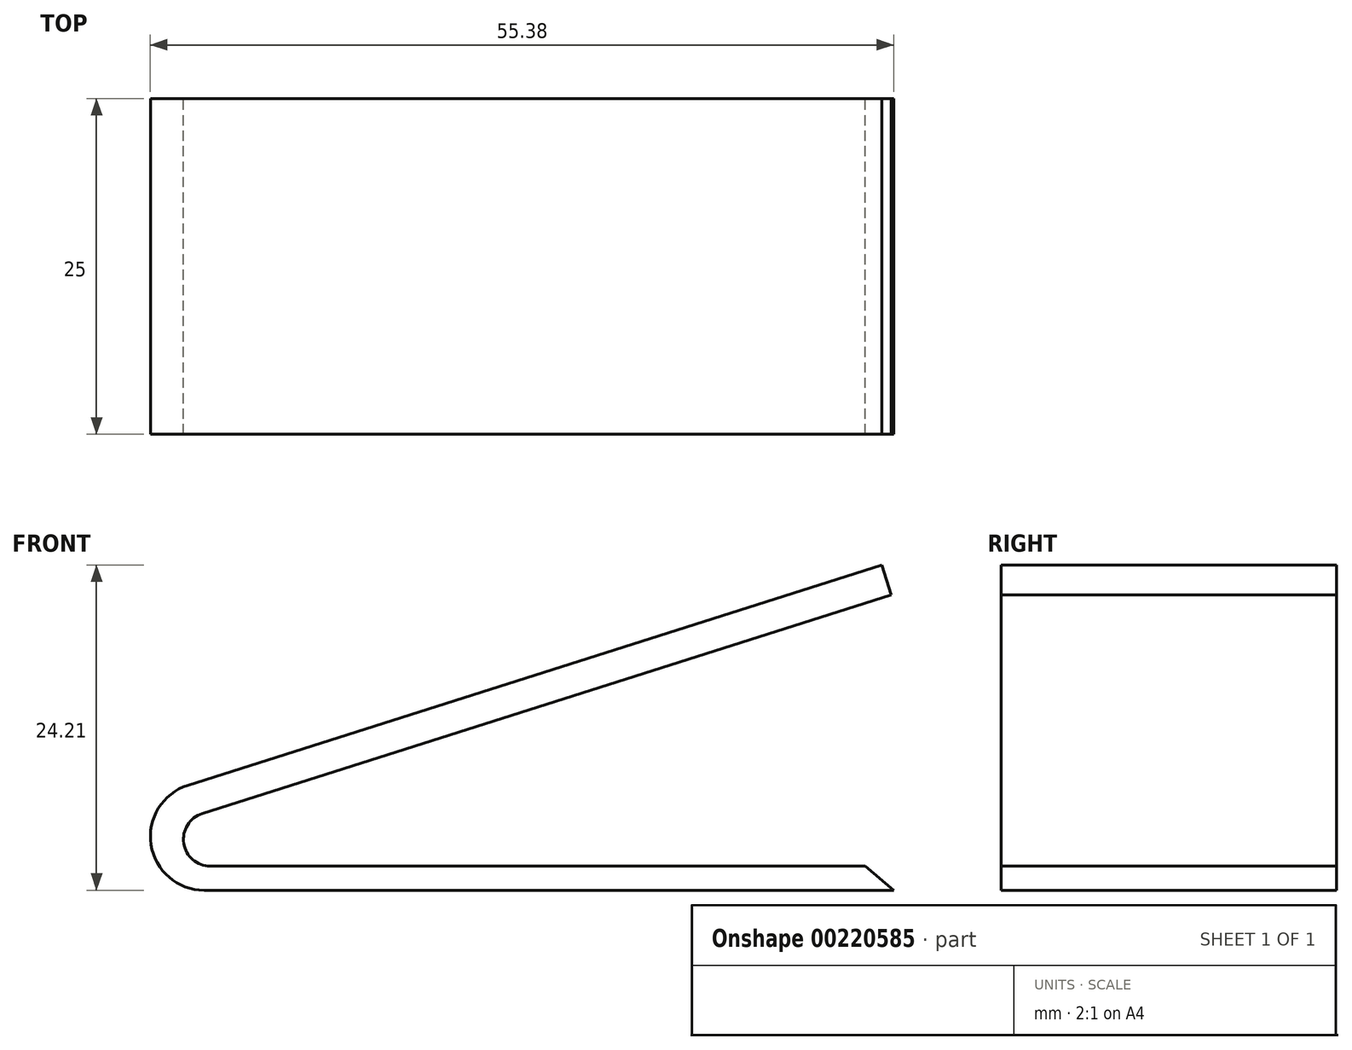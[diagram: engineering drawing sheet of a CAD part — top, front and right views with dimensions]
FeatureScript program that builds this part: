
annotation { "Feature Type Name" : "Feature", "Feature Type Description" : "" }
export const myFeature = defineFeature(function(context is Context, id is Id, definition is map)
    precondition{}
    {
        {
            var Q0;
            Q0=qCreatedBy(makeId("Front.planeOp"),FACE);
            var sketch = newSketch(context, id + "F0", { "sketchPlane" : qUnion([Q0])});
            skLineSegment(sketch, "E0", {"start": v(25.84, 0) * mm, "end": v(77.22, 0) * mm});
            skLineSegment(sketch, "E1", {"start": v(24.63, 7.81) * mm, "end": v(76.33, 24.2) * mm});
            skLineSegment(sketch, "E2", {"start": v(76.33, 24.2) * mm, "end": v(77.03, 21.98) * mm});
            skLineSegment(sketch, "E3", {"start": v(77.03, 21.98) * mm, "end": v(25.7, 5.7) * mm});
            skLineSegment(sketch, "E4", {"start": v(26.3, 1.8) * mm, "end": v(75.1, 1.8) * mm});
            skLineSegment(sketch, "E5", {"start": v(75.1, 1.8) * mm, "end": v(77.22, 0) * mm});
            skPoint(sketch, "E6.visualSharp", {"position": v(13.39, 1.8) * mm});
            skArc(sketch, "E6.filletArc", {"start": v(25.7, 5.7) * mm, "mid": v(24.33, 3.5) * mm, "end": v(26.3, 1.8) * mm});
            skPoint(sketch, "E7.visualSharp", {"position": v(0, 0) * mm});
            skArc(sketch, "E7.filletArc", {"start": v(24.63, 7.81) * mm, "mid": v(21.9, 3.39) * mm, "end": v(25.84, 0) * mm});
            skSolve(sketch);
        }
        {
            var Q0;
            Q0 = qSketchRegion(id + "F0", true);
            extrude(context, id + "F1", {"entities" : qUnion([Q0]), "depth" : 25 * mm});
        }
    });
